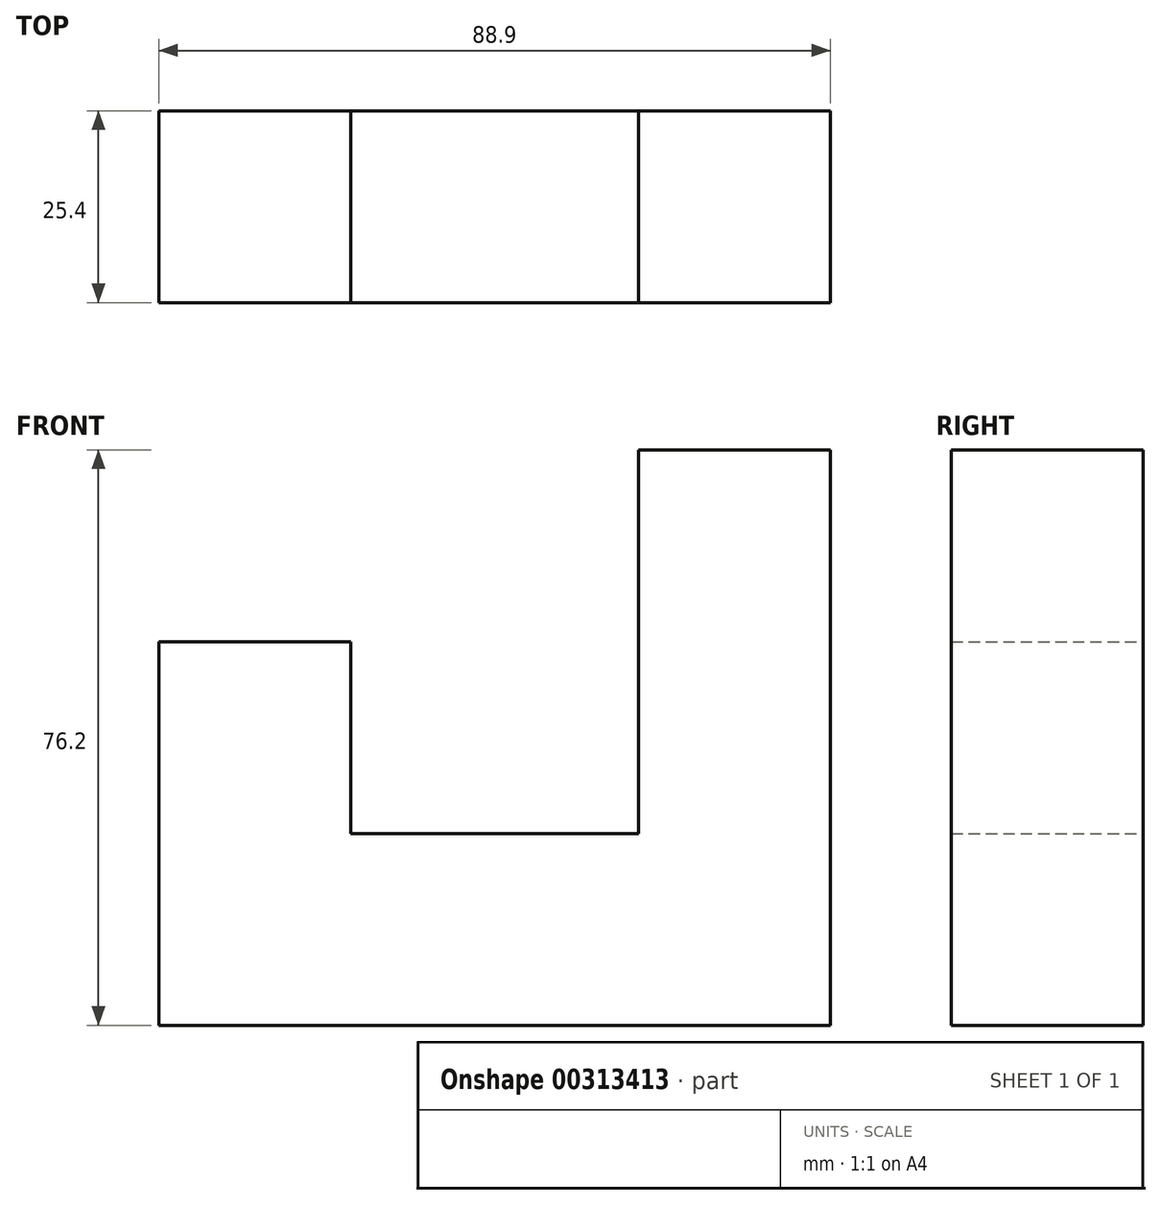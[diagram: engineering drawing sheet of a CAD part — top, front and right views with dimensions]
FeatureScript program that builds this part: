
annotation { "Feature Type Name" : "Feature", "Feature Type Description" : "" }
export const myFeature = defineFeature(function(context is Context, id is Id, definition is map)
    precondition{}
    {
        {
            var Q0;
            Q0=qCreatedBy(makeId("Front.planeOp"),FACE);
            var sketch = newSketch(context, id + "F0", { "sketchPlane" : qUnion([Q0])});
            skLineSegment(sketch, "E0", {"start": v(-38.54, -45.29) * mm, "end": v(50.36, -45.29) * mm});
            skLineSegment(sketch, "E1", {"start": v(50.36, -45.29) * mm, "end": v(50.36, 30.91) * mm});
            skLineSegment(sketch, "E2", {"start": v(50.36, 30.91) * mm, "end": v(24.96, 30.91) * mm});
            skLineSegment(sketch, "E3", {"start": v(24.96, 30.91) * mm, "end": v(24.96, -19.89) * mm});
            skLineSegment(sketch, "E4", {"start": v(24.96, -19.89) * mm, "end": v(-13.14, -19.89) * mm});
            skLineSegment(sketch, "E5", {"start": v(-13.14, -19.89) * mm, "end": v(-13.14, 5.51) * mm});
            skLineSegment(sketch, "E6", {"start": v(-13.14, 5.51) * mm, "end": v(-38.54, 5.51) * mm});
            skLineSegment(sketch, "E7", {"start": v(-38.54, 5.51) * mm, "end": v(-38.54, -45.29) * mm});
            skSolve(sketch);
        }
        {
            var Q0;
            Q0=makeQuery(id+"F0.imprint","IMPRINT",FACE,{"disambiguationData":[TD([[makeQuery(id+"F0.imprint","IMPRINT",EDGE,{"derivedFrom":sQuery(id+"F0.wireOp",EDGE,"E0")}),1.0]])]});
            extrude(context, id + "F1", {"entities" : qUnion([Q0]), "depth" : 25.4 * mm});
        }
    });
